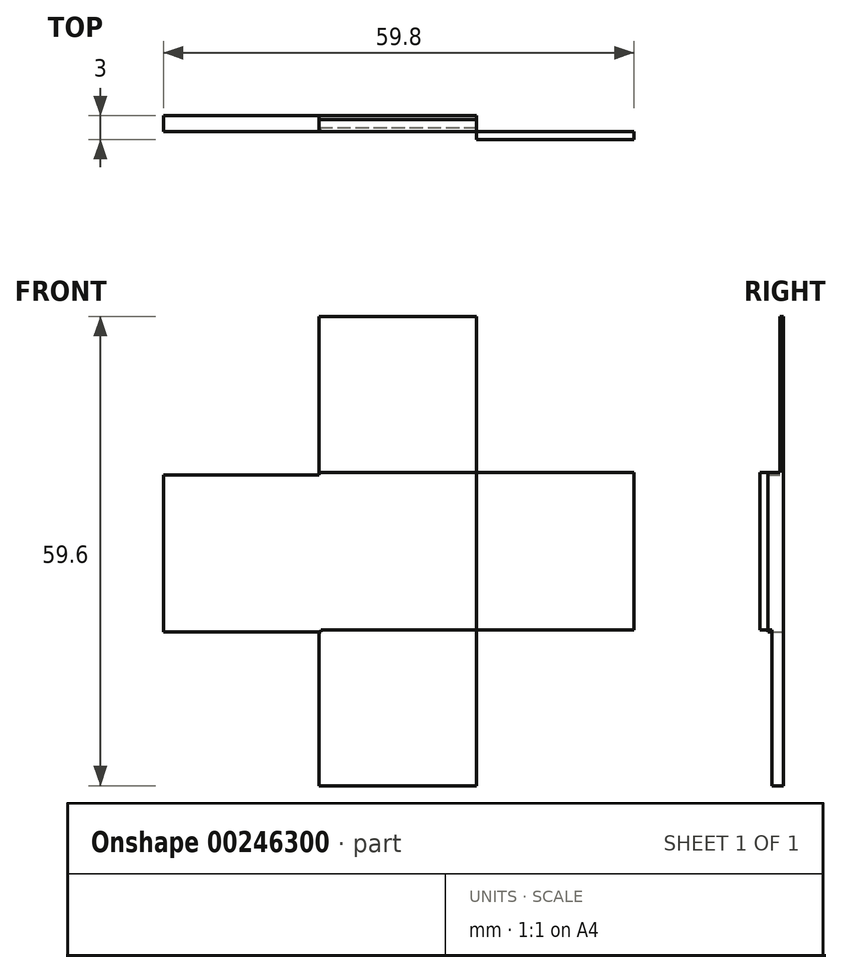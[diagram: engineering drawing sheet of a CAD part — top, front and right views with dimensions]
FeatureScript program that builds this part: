
annotation { "Feature Type Name" : "Feature", "Feature Type Description" : "" }
export const myFeature = defineFeature(function(context is Context, id is Id, definition is map)
    precondition{}
    {
        {
            var Q0;
            Q0=qCreatedBy(makeId("Front.planeOp"),FACE);
            var sketch = newSketch(context, id + "F0", { "sketchPlane" : qUnion([Q0])});
            skLineSegment(sketch, "E0.bottom", {"start": v(-10, 10) * mm, "end": v(10, 10) * mm});
            skLineSegment(sketch, "E0.top", {"start": v(-10, -10) * mm, "end": v(10, -10) * mm});
            skLineSegment(sketch, "E0.left", {"start": v(-10, 10) * mm, "end": v(-10, -10) * mm});
            skLineSegment(sketch, "E0.right", {"start": v(10, 10) * mm, "end": v(10, -10) * mm});
            skPoint(sketch, "E0.middle", {"position": v(0, 0) * mm});
            skSolve(sketch);
        }
        {
            var Q0;
            Q0 = qSketchRegion(id + "F0", true);
            extrude(context, id + "F1", {"entities" : qUnion([Q0]), "depth" : 2 * mm});
        }
        {
            var Q0;
            Q0=qCreatedBy(makeId("Front.planeOp"),FACE);
            var sketch = newSketch(context, id + "F2", { "sketchPlane" : qUnion([Q0])});
            skLineSegment(sketch, "E1.bottom", {"start": v(-10, 9.8) * mm, "end": v(10, 9.8) * mm});
            skLineSegment(sketch, "E1.top", {"start": v(-10, 29.8) * mm, "end": v(10, 29.8) * mm});
            skLineSegment(sketch, "E1.left", {"start": v(-10, 9.8) * mm, "end": v(-10, 29.8) * mm});
            skLineSegment(sketch, "E1.right", {"start": v(10, 9.8) * mm, "end": v(10, 29.8) * mm});
            skSolve(sketch);
        }
        {
            var Q0;
            Q0 = qSketchRegion(id + "F2", true);
            extrude(context, id + "F3", {"entities" : qUnion([Q0]), "operationType" : NewBodyOperationType.ADD, "depth" : 0.5 * mm});
        }
        {
            var Q0;
            Q0=makeQuery(id+"F1.opExtrude","CAP_FACE",FACE,{"disambiguationData":[OSD([sQuery(id+"F0.wireOp",EDGE,"E0.bottom"),sQuery(id+"F0.wireOp",EDGE,"E0.top"),sQuery(id+"F0.wireOp",EDGE,"E0.left"),sQuery(id+"F0.wireOp",EDGE,"E0.right")])],"isStart":false});
            var sketch = newSketch(context, id + "F4", { "sketchPlane" : qUnion([Q0])});
            skLineSegment(sketch, "E2.bottom", {"start": v(10, 10) * mm, "end": v(30, 10) * mm});
            skLineSegment(sketch, "E2.top", {"start": v(10, -10) * mm, "end": v(30, -10) * mm});
            skLineSegment(sketch, "E2.left", {"start": v(10, 10) * mm, "end": v(10, -10) * mm});
            skLineSegment(sketch, "E2.right", {"start": v(30, 10) * mm, "end": v(30, -10) * mm});
            skSolve(sketch);
        }
        {
            var Q0;
            Q0 = qSketchRegion(id + "F4", true);
            extrude(context, id + "F5", {"entities" : qUnion([Q0]), "depth" : 1 * mm});
        }
        {
            var Q0;
            Q0=qCreatedBy(makeId("Front.planeOp"),FACE);
            var sketch = newSketch(context, id + "F6", { "sketchPlane" : qUnion([Q0])});
            skLineSegment(sketch, "E3.bottom", {"start": v(-10, -9.8) * mm, "end": v(10, -9.8) * mm});
            skLineSegment(sketch, "E3.top", {"start": v(-10, -29.8) * mm, "end": v(10, -29.8) * mm});
            skLineSegment(sketch, "E3.left", {"start": v(-10, -9.8) * mm, "end": v(-10, -29.8) * mm});
            skLineSegment(sketch, "E3.right", {"start": v(10, -9.8) * mm, "end": v(10, -29.8) * mm});
            skSolve(sketch);
        }
        {
            var Q0;
            Q0 = qSketchRegion(id + "F6", true);
            extrude(context, id + "F7", {"entities" : qUnion([Q0]), "operationType" : NewBodyOperationType.ADD, "depth" : 1.5 * mm});
        }
        {
            var Q0;
            Q0=qCreatedBy(makeId("Front.planeOp"),FACE);
            var sketch = newSketch(context, id + "F8", { "sketchPlane" : qUnion([Q0])});
            skLineSegment(sketch, "E4.bottom", {"start": v(-9.8, 9.7) * mm, "end": v(-29.8, 9.7) * mm});
            skLineSegment(sketch, "E4.top", {"start": v(-9.8, -10.3) * mm, "end": v(-29.8, -10.3) * mm});
            skLineSegment(sketch, "E4.left", {"start": v(-9.8, 9.7) * mm, "end": v(-9.8, -10.3) * mm});
            skLineSegment(sketch, "E4.right", {"start": v(-29.8, 9.7) * mm, "end": v(-29.8, -10.3) * mm});
            skSolve(sketch);
        }
        {
            var Q0;
            Q0 = qSketchRegion(id + "F8", true);
            extrude(context, id + "F9", {"entities" : qUnion([Q0]), "operationType" : NewBodyOperationType.ADD, "depth" : 2 * mm});
        }
    });
